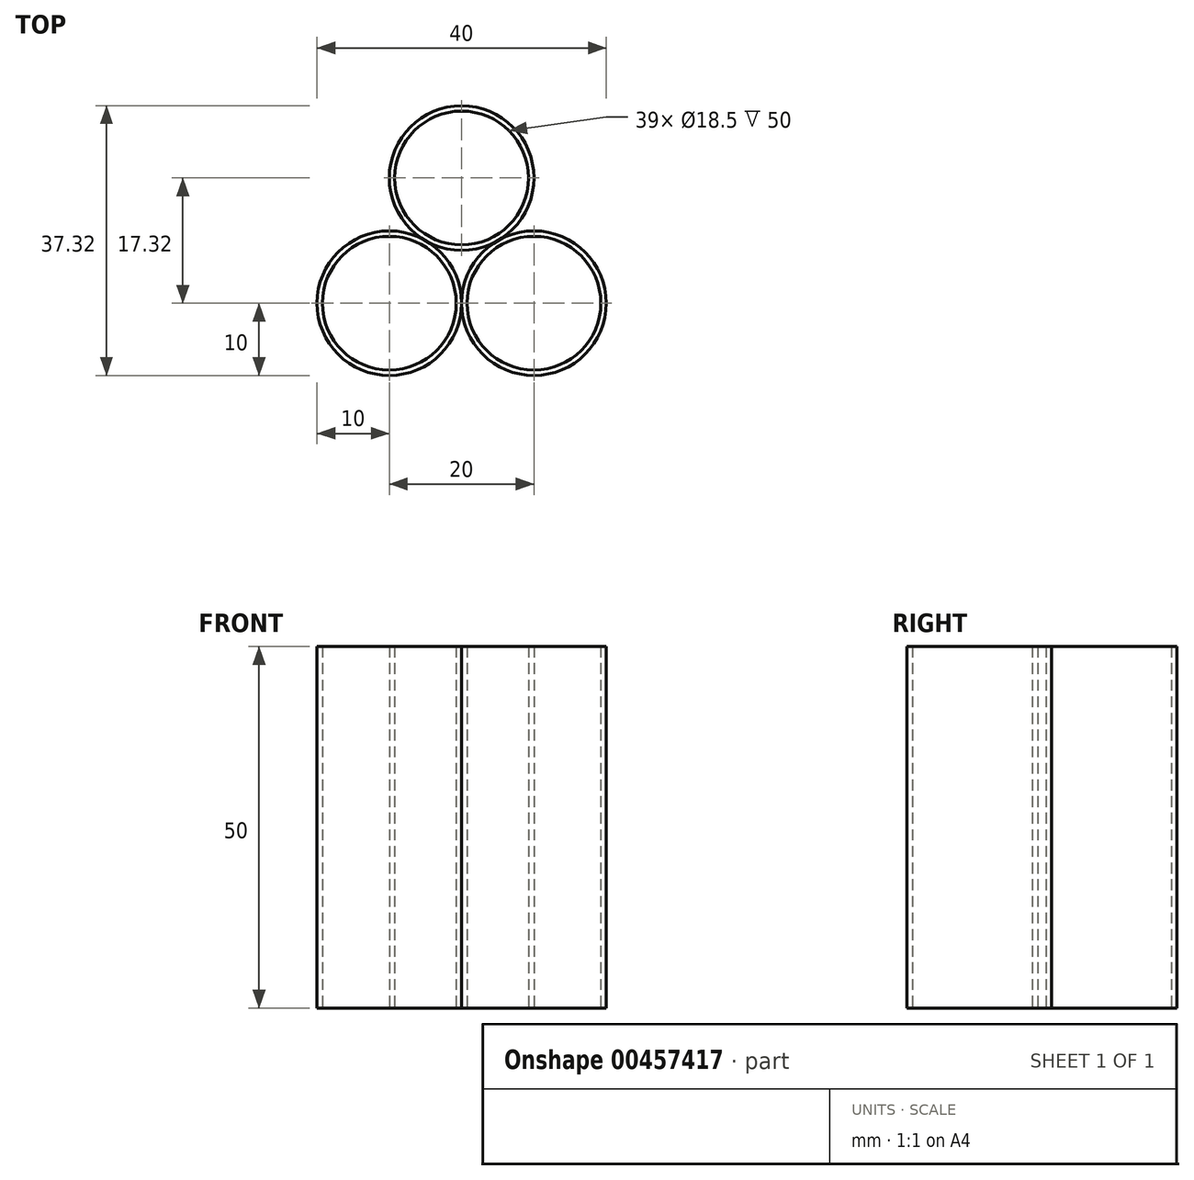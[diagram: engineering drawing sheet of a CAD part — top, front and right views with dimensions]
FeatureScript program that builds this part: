
annotation { "Feature Type Name" : "Feature", "Feature Type Description" : "" }
export const myFeature = defineFeature(function(context is Context, id is Id, definition is map)
    precondition{}
    {
        {
            var Q0;
            Q0=qCreatedBy(makeId("Top.planeOp"),FACE);
            var sketch = newSketch(context, id + "F0", { "sketchPlane" : qUnion([Q0])});
            skLineSegment(sketch, "E0", {"start": v(0, 0) * mm, "end": v(10, 17.32) * mm, "construction": true});
            skLineSegment(sketch, "E1", {"start": v(0, 0) * mm, "end": v(20, 0) * mm, "construction": true});
            skLineSegment(sketch, "E2", {"start": v(20, 0) * mm, "end": v(10, 17.32) * mm, "construction": true});
            skCircle(sketch, "E3", {"center": v(0, 0) * mm, "radius": 10 * mm});
            skCircle(sketch, "E4", {"center": v(20, 0) * mm, "radius": 10 * mm});
            skCircle(sketch, "E5", {"center": v(10, 17.32) * mm, "radius": 10 * mm});
            skCircle(sketch, "E6.0", {"center": v(10, 17.32) * mm, "radius": 9.25 * mm});
            skCircle(sketch, "E7.0", {"center": v(0, 0) * mm, "radius": 9.25 * mm});
            skCircle(sketch, "E8.0", {"center": v(20, 0) * mm, "radius": 9.25 * mm});
            skSolve(sketch);
        }
        {
            var Q0;
            Q0=makeQuery(id+"F0.imprint","IMPRINT",FACE,{"disambiguationData":[TD([[makeQuery(id+"F0.imprint","IMPRINT",EDGE,{"derivedFrom":sQuery(id+"F0.wireOp",EDGE,"E6.0")}),-1.0]])]});
            var Q1;
            Q1=makeQuery(id+"F0.imprint","IMPRINT",FACE,{"disambiguationData":[TD([[makeQuery(id+"F0.imprint","IMPRINT",EDGE,{"derivedFrom":sQuery(id+"F0.wireOp",EDGE,"E8.0")}),-1.0]])]});
            var Q2;
            Q2=makeQuery(id+"F0.imprint","IMPRINT",FACE,{"disambiguationData":[TD([[makeQuery(id+"F0.imprint","IMPRINT",EDGE,{"derivedFrom":sQuery(id+"F0.wireOp",EDGE,"E7.0")}),-1.0]])]});
            extrude(context, id + "F1", {"entities" : qUnion([Q0, Q1, Q2]), "depth" : 50 * mm, "offsetDistance" : 25 * mm});
        }
    });
